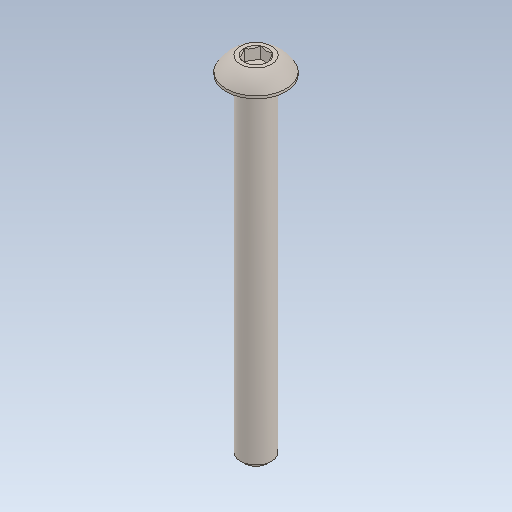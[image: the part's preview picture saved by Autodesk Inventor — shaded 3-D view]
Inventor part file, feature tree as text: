
AUTODESK INVENTOR PART (.ipt)
format: ipt  version: 2020 (Build 240168000, 168)  size: 110,592 bytes
history: native  units: in
note: dims shown in document units (in); Inventor stores cm internally (conversion verified against a paired STEP export)
features: fillet x1
ambient origin geometry x8: Origin, YZ Plane, XZ Plane, XY Plane, X Axis, Y Axis, Z Axis, Center Point
bodies: Solid1 (feature_tree)
feature tree (1):
  fillet  "Fillet1"  [1 undecoded]
note: 1 required parameter value undecoded (feature->parameter linkage not recoverable at this tier; creation-order binding heuristic only, values carry confidence <= 0.55)
